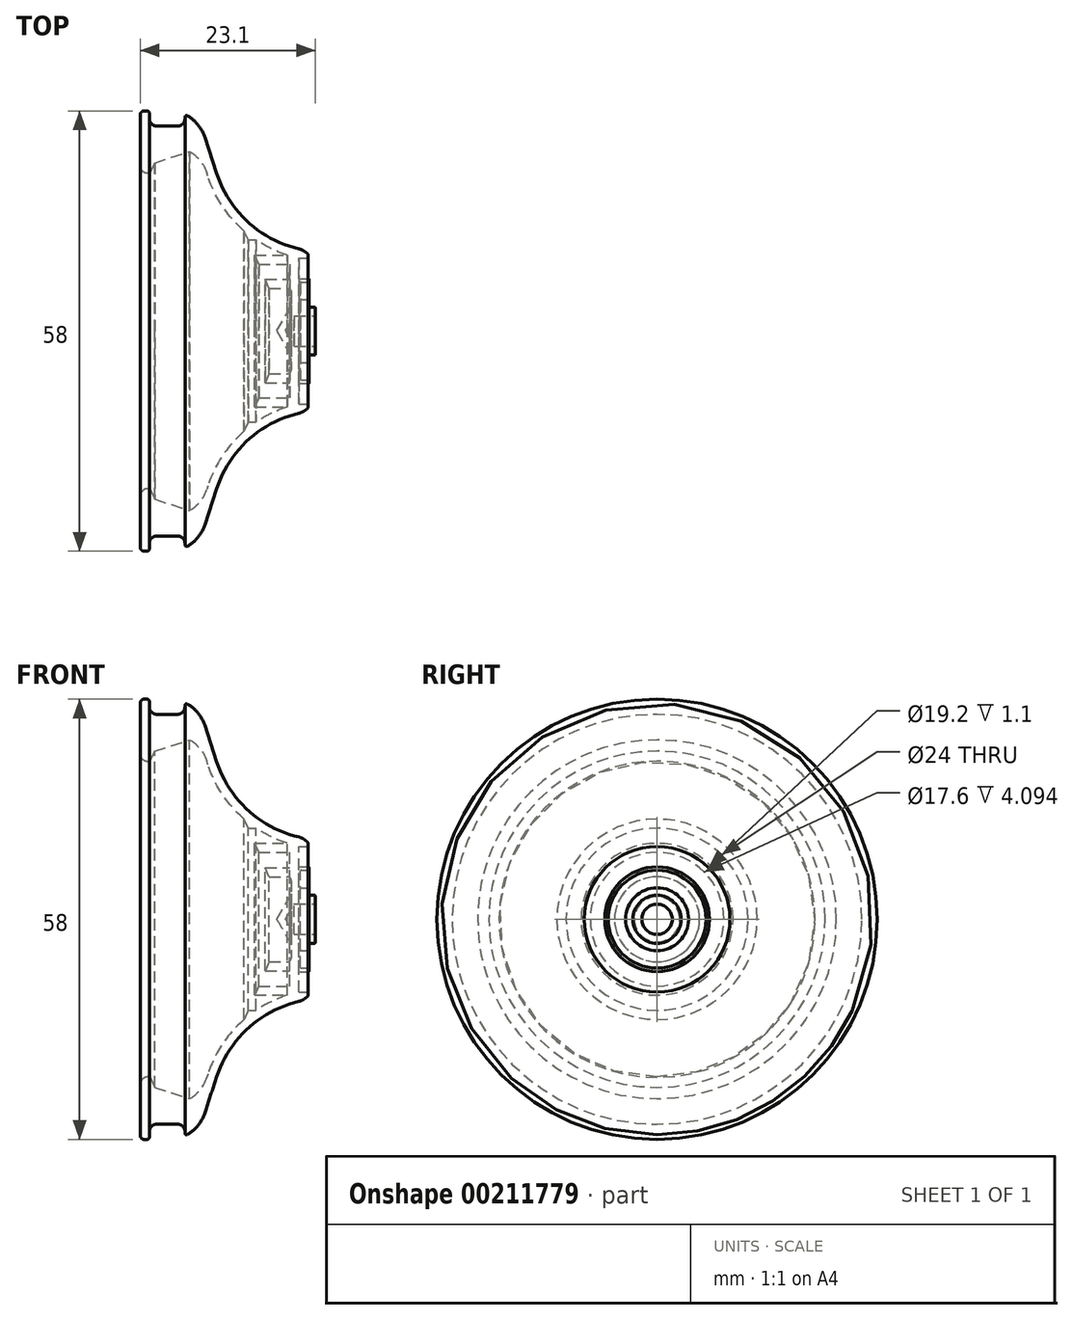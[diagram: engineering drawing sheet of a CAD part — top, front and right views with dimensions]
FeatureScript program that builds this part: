
annotation { "Feature Type Name" : "Feature", "Feature Type Description" : "" }
export const myFeature = defineFeature(function(context is Context, id is Id, definition is map)
    precondition{}
    {
        {
            var Q0;
            Q0=qCreatedBy(makeId("Front.planeOp"),FACE);
            var sketch = newSketch(context, id + "F0", { "sketchPlane" : qUnion([Q0])});
            skLineSegment(sketch, "E0", {"start": v(-1.4, 2) * mm, "end": v(-4.2, 2) * mm});
            skLineSegment(sketch, "E1", {"start": v(-4.2, 2) * mm, "end": v(-5.35, 0) * mm});
            skLineSegment(sketch, "E2", {"start": v(-5.35, 0) * mm, "end": v(-6.5, 0) * mm});
            skLineSegment(sketch, "E3", {"start": v(-6.5, 0) * mm, "end": v(-4.79, 2.98) * mm});
            skLineSegment(sketch, "E4", {"start": v(-4.6, 5.6) * mm, "end": v(-7.5, 5.6) * mm});
            skLineSegment(sketch, "E5", {"start": v(-7.5, 5.6) * mm, "end": v(-8.03, 6.8) * mm});
            skLineSegment(sketch, "E6", {"start": v(-24.5, 21.77) * mm, "end": v(-24.5, 29) * mm});
            skLineSegment(sketch, "E7", {"start": v(-24.5, 29) * mm, "end": v(-23.6, 29) * mm});
            skLineSegment(sketch, "E8", {"start": v(-1.4, 3.17) * mm, "end": v(-2.4, 3.17) * mm});
            skLineSegment(sketch, "E9", {"start": v(-2.4, 3.17) * mm, "end": v(-2.4, 4.15) * mm});
            skLineSegment(sketch, "E10", {"start": v(-2.4, 4.15) * mm, "end": v(-3.4, 4.15) * mm});
            skLineSegment(sketch, "E11", {"start": v(-3.4, 4.15) * mm, "end": v(-3.4, 6.45) * mm});
            skLineSegment(sketch, "E12", {"start": v(-3.4, 6.45) * mm, "end": v(-2.25, 6.45) * mm});
            skLineSegment(sketch, "E13", {"start": v(-2.25, 6.45) * mm, "end": v(-2.25, 6.9) * mm});
            skLineSegment(sketch, "E14", {"start": v(-2.25, 6.9) * mm, "end": v(-3.6, 6.9) * mm});
            skLineSegment(sketch, "E15", {"start": v(-3.6, 6.9) * mm, "end": v(-3.6, 9.6) * mm});
            skLineSegment(sketch, "E16", {"start": v(-3.6, 9.6) * mm, "end": v(-2.4, 9.6) * mm});
            skLineSegment(sketch, "E17", {"start": v(-2.4, 9.6) * mm, "end": v(-2.4, 10.6) * mm});
            skLineSegment(sketch, "E18", {"start": v(-1.4, 3.17) * mm, "end": v(-1.4, 2) * mm});
            skLineSegment(sketch, "E19", {"start": v(-2.4, 10.6) * mm, "end": v(-2.4, 10.6) * mm});
            skLineSegment(sketch, "E20", {"start": v(-4.6, 5.6) * mm, "end": v(-4.6, 3.17) * mm});
            skLineSegment(sketch, "E21", {"start": v(-4.6, 3.17) * mm, "end": v(-4.79, 2.98) * mm});
            skLineSegment(sketch, "E22", {"start": v(-16, 25.55) * mm, "end": v(-14.44, 20.77) * mm});
            skArc(sketch, "E23.filletArc", {"start": v(-14.44, 20.77) * mm, "mid": v(-9.86, 13.98) * mm, "end": v(-2.4, 10.6) * mm});
            skPoint(sketch, "E24.visualSharp", {"position": v(-17.13, 29) * mm});
            skArc(sketch, "E24.filletArc", {"start": v(-16, 25.55) * mm, "mid": v(-16.89, 27.17) * mm, "end": v(-18.3, 28.36) * mm});
            skPoint(sketch, "E25.visualSharp", {"position": v(-15.72, 24.57) * mm});
            skPoint(sketch, "E26.visualSharp", {"position": v(-24.5, 21.22) * mm});
            skLineSegment(sketch, "E27", {"start": v(-23.3, 28.7) * mm, "end": v(-23.3, 28) * mm});
            skLineSegment(sketch, "E28", {"start": v(-22.3, 27) * mm, "end": v(-19.6, 27) * mm});
            skLineSegment(sketch, "E29", {"start": v(-18.6, 28) * mm, "end": v(-18.6, 28.18) * mm});
            skPoint(sketch, "E30.visualSharp", {"position": v(-23.3, 27) * mm});
            skArc(sketch, "E30.filletArc", {"start": v(-23.3, 28) * mm, "mid": v(-23, 27.3) * mm, "end": v(-22.3, 27) * mm});
            skPoint(sketch, "E31.visualSharp", {"position": v(-18.6, 27) * mm});
            skArc(sketch, "E31.filletArc", {"start": v(-19.6, 27) * mm, "mid": v(-18.9, 27.3) * mm, "end": v(-18.6, 28) * mm});
            skPoint(sketch, "E32.visualSharp", {"position": v(-23.3, 29) * mm});
            skArc(sketch, "E32.filletArc", {"start": v(-23.3, 28.7) * mm, "mid": v(-23.39, 28.91) * mm, "end": v(-23.6, 29) * mm});
            skPoint(sketch, "E33.visualSharp", {"position": v(-18.6, 28.51) * mm});
            skArc(sketch, "E33.filletArc", {"start": v(-18.3, 28.36) * mm, "mid": v(-18.5, 28.36) * mm, "end": v(-18.6, 28.18) * mm});
            skArc(sketch, "E34.filletArc", {"start": v(-24.5, 21.77) * mm, "mid": v(-24.09, 20.96) * mm, "end": v(-23.2, 20.82) * mm});
            skArc(sketch, "E35.filletArc", {"start": v(-15.58, 20.4) * mm, "mid": v(-14.56, 17.97) * mm, "end": v(-13.16, 15.74) * mm});
            skLineSegment(sketch, "E36", {"start": v(-4.8, 6.8) * mm, "end": v(-4.8, 8.8) * mm});
            skLineSegment(sketch, "E37", {"start": v(-8.03, 6.8) * mm, "end": v(-4.8, 6.8) * mm});
            skLineSegment(sketch, "E38", {"start": v(-8.9, 8.8) * mm, "end": v(-4.8, 8.8) * mm});
            skLineSegment(sketch, "E39", {"start": v(-9.41, 10) * mm, "end": v(-5.1, 10) * mm});
            skLineSegment(sketch, "E40", {"start": v(-10.28, 12) * mm, "end": v(-9.23, 12) * mm});
            skLineSegment(sketch, "E41.trimOffspring", {"start": v(-8.9, 8.8) * mm, "end": v(-9.41, 10) * mm});
            skLineSegment(sketch, "E42.trimOffspring", {"start": v(-10.28, 12) * mm, "end": v(-10.8, 13.2) * mm});
            skLineSegment(sketch, "E43", {"start": v(-10.8, 13.2) * mm, "end": v(-10.8, 13.2) * mm});
            skArc(sketch, "E44.trimOffspring", {"start": v(-9.23, 12) * mm, "mid": v(-7.24, 10.85) * mm, "end": v(-5.1, 10) * mm});
            skLineSegment(sketch, "E45", {"start": v(-15.73, 20.86) * mm, "end": v(-15.58, 20.4) * mm});
            skArc(sketch, "E46.trimOffspring", {"start": v(-13.16, 15.74) * mm, "mid": v(-12.05, 14.4) * mm, "end": v(-10.8, 13.2) * mm});
            skPoint(sketch, "E47.visualSharp", {"position": v(-16.84, 24.25) * mm});
            skArc(sketch, "E47.filletArc", {"start": v(-15.73, 20.86) * mm, "mid": v(-16.6, 22.46) * mm, "end": v(-17.99, 23.64) * mm});
            skLineSegment(sketch, "E48", {"start": v(-23.2, 20.82) * mm, "end": v(-22.58, 22.16) * mm});
            skLineSegment(sketch, "E49", {"start": v(-22.58, 22.16) * mm, "end": v(-17.99, 23.64) * mm});
            skSolve(sketch);
        }
        {
            var Q0;
            Q0=qSketchRegion(id+"F0",true);
            var Q1;
            Q1=sQuery(id+"F0.wireOp",EDGE,"E2");
            revolve(context, id + "F1", {"entities" : qUnion([Q0]), "axis" : qUnion([Q1]), "revolveType" : RevolveType.FULL});
        }
        {
            var Q0;
            Q0=makeQuery(id+"F1.opRevolve","SWEPT_EDGE",EDGE,{"disambiguationData":[OSD([sQuery(id+"F0.wireOp",EDGE,"E17"),sQuery(id+"F0.wireOp",EDGE,"E23.filletArc")])]});
            chamfer(context, id + "F2", {"entities" : qUnion([Q0]), "chamferType" : ChamferType.TWO_OFFSETS, "width1" : 0.5 * mm, "oppositeDirection" : false, "width2" : 0.8 * mm, "tangentPropagation" : true});
        }
        {
            var Q0;
            Q0=makeQuery(id+"F2.opChamfer","BLEND_EDGE",EDGE,{"blendedFrom":[makeQuery(id+"F1.opRevolve","SWEPT_EDGE",EDGE,{"disambiguationData":[OSD([sQuery(id+"F0.wireOp",EDGE,"E17"),sQuery(id+"F0.wireOp",EDGE,"E19")])]}),makeQuery(id+"F1.opRevolve","SWEPT_FACE",FACE,{"disambiguationData":[OSD([sQuery(id+"F0.wireOp",EDGE,"E23.filletArc")])]})],"blendedInto":[makeQuery(id+"F1.opRevolve","SWEPT_FACE",FACE,{"disambiguationData":[OSD([sQuery(id+"F0.wireOp",EDGE,"E23.filletArc")])]})]});
            fillet(context, id + "F3", {"entities" : qUnion([Q0]), "radius" : 2 * mm, "tangentPropagation" : true, "allowEdgeOverflow" : false});
        }
        {
            var Q0;
            {var subQ0=sQuery(id+"F0.wireOp",EDGE,"E17");Q0=makeQuery(id+"F2.opChamfer","BLEND_EDGE",EDGE,{"blendedFrom":[makeQuery(id+"F1.opRevolve","SWEPT_EDGE",EDGE,{"disambiguationData":[OSD([subQ0,sQuery(id+"F0.wireOp",EDGE,"E19")])]}),makeQuery(id+"F1.opRevolve","SWEPT_FACE",FACE,{"disambiguationData":[OSD([subQ0])]})],"blendedInto":[makeQuery(id+"F1.opRevolve","SWEPT_FACE",FACE,{"disambiguationData":[OSD([subQ0])]})]});}
            fillet(context, id + "F4", {"entities" : qUnion([Q0]), "radius" : 0.2 * mm, "tangentPropagation" : true, "allowEdgeOverflow" : false});
        }
        {
            var Q0;
            Q0=makeQuery(id+"F1.opRevolve","SWEPT_EDGE",EDGE,{"disambiguationData":[OSD([sQuery(id+"F0.wireOp",EDGE,"E9"),sQuery(id+"F0.wireOp",EDGE,"E10")])]});
            var Q1;
            Q1=makeQuery(id+"F1.opRevolve","SWEPT_EDGE",EDGE,{"disambiguationData":[OSD([sQuery(id+"F0.wireOp",EDGE,"E10"),sQuery(id+"F0.wireOp",EDGE,"E11")])]});
            var Q2;
            Q2=makeQuery(id+"F1.opRevolve","SWEPT_EDGE",EDGE,{"disambiguationData":[OSD([sQuery(id+"F0.wireOp",EDGE,"E12"),sQuery(id+"F0.wireOp",EDGE,"E13")])]});
            var Q3;
            Q3=makeQuery(id+"F1.opRevolve","SWEPT_EDGE",EDGE,{"disambiguationData":[OSD([sQuery(id+"F0.wireOp",EDGE,"E13"),sQuery(id+"F0.wireOp",EDGE,"E14")])]});
            var Q4;
            Q4=makeQuery(id+"F1.opRevolve","SWEPT_EDGE",EDGE,{"disambiguationData":[OSD([sQuery(id+"F0.wireOp",EDGE,"E16"),sQuery(id+"F0.wireOp",EDGE,"E17")])]});
            var Q5;
            Q5=makeQuery(id+"F1.opRevolve","SWEPT_EDGE",EDGE,{"disambiguationData":[OSD([sQuery(id+"F0.wireOp",EDGE,"E11"),sQuery(id+"F0.wireOp",EDGE,"E12")])]});
            var Q6;
            Q6=makeQuery(id+"F1.opRevolve","SWEPT_EDGE",EDGE,{"disambiguationData":[OSD([sQuery(id+"F0.wireOp",EDGE,"E8"),sQuery(id+"F0.wireOp",EDGE,"E9")])]});
            fillet(context, id + "F5", {"entities" : qUnion([Q0, Q1, Q2, Q3, Q4, Q5, Q6]), "radius" : 0.1 * mm, "tangentPropagation" : true, "allowEdgeOverflow" : false});
        }
        {
            var Q0;
            Q0=makeQuery(id+"F1.opRevolve","SWEPT_EDGE",EDGE,{"disambiguationData":[OSD([sQuery(id+"F0.wireOp",EDGE,"E8"),sQuery(id+"F0.wireOp",EDGE,"E18")])]});
            fillet(context, id + "F6", {"entities" : qUnion([Q0]), "radius" : 0.2 * mm, "tangentPropagation" : true, "allowEdgeOverflow" : false});
        }
        {
            var Q0;
            Q0=makeQuery(id+"F1.opRevolve","SWEPT_EDGE",EDGE,{"disambiguationData":[OSD([sQuery(id+"F0.wireOp",EDGE,"E6"),sQuery(id+"F0.wireOp",EDGE,"E7")])]});
            fillet(context, id + "F7", {"entities" : qUnion([Q0]), "radius" : 0.5 * mm, "tangentPropagation" : true, "allowEdgeOverflow" : false});
        }
        {
            var Q0;
            Q0=makeQuery(id+"F1.opRevolve","SWEPT_EDGE",EDGE,{"disambiguationData":[OSD([sQuery(id+"F0.wireOp",EDGE,"E20"),sQuery(id+"F0.wireOp",EDGE,"qzoH6j8X-IBxw-pTTz-kvqH-HLydLYGYBeqi")])]});
            fillet(context, id + "F8", {"entities" : qUnion([Q0]), "radius" : 0.5 * mm, "tangentPropagation" : true, "allowEdgeOverflow" : false});
        }
    });
